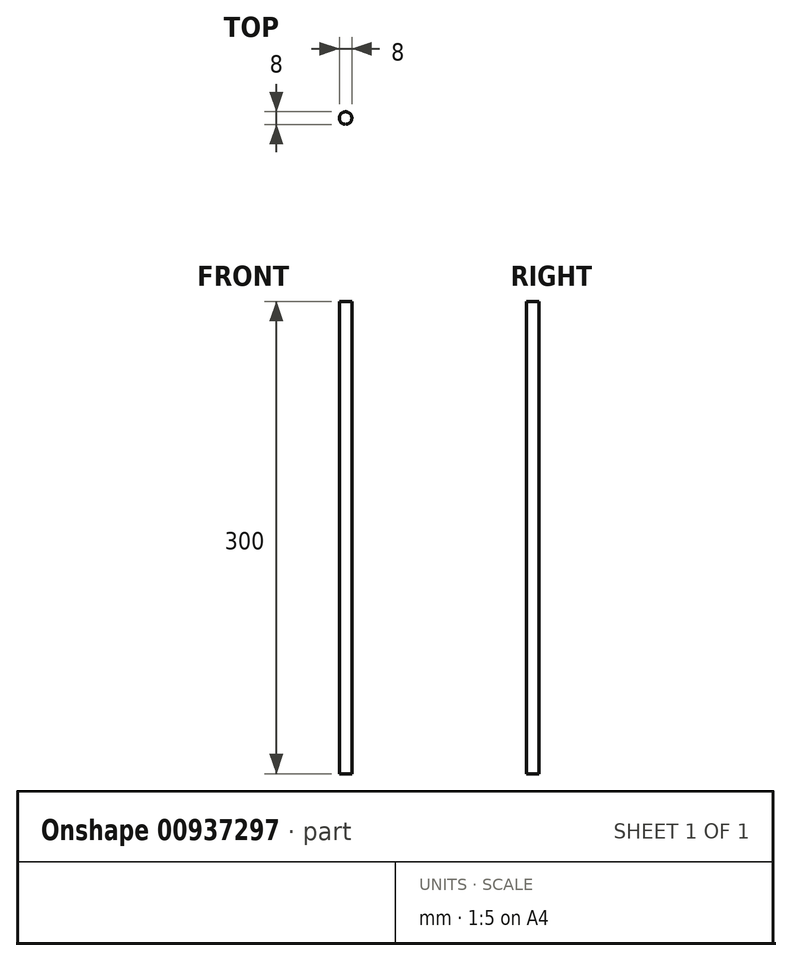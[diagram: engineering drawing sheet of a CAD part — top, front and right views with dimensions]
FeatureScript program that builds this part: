
annotation { "Feature Type Name" : "Feature", "Feature Type Description" : "" }
export const myFeature = defineFeature(function(context is Context, id is Id, definition is map)
    precondition{}
    {
        {
            var Q0;
            Q0=qCreatedBy(makeId("Top.planeOp"),FACE);
            var sketch = newSketch(context, id + "F0", { "sketchPlane" : qUnion([Q0])});
            skCircle(sketch, "E0", {"center": v(0, 0) * mm, "radius": 4 * mm});
            skSolve(sketch);
        }
        {
            var Q0;
            Q0=makeQuery(id+"F0.imprint","IMPRINT",FACE,{"disambiguationData":[TD([[makeQuery(id+"F0.imprint","IMPRINT",EDGE,{"derivedFrom":sQuery(id+"F0.wireOp",EDGE,"E0")}),1.0]])]});
            extrude(context, id + "F1", {"entities" : qUnion([Q0]), "depth" : 300 * mm, "offsetDistance" : 25.4 * mm});
        }
    });
